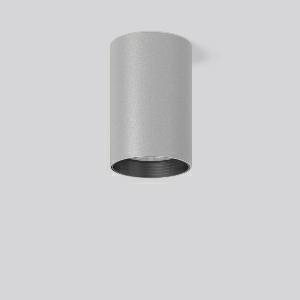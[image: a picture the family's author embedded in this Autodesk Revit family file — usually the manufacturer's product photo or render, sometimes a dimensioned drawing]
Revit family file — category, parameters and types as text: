
# Revit family: heledon_maxi_a_931243_004_76_f6dd
name_source: partatom
category: Lighting Fixtures
units: mm (PartAtom-declared; Revit-internal decimal feet)

## family parameters
Cut with Voids When Loaded = No
Host = Face
Light Source = No
Part Type = Normal
Room Calculation Point = No
Round Connector Dimension = Use Diameter
Shared = No

## types (1)
- HELEDON maxi A (1 x LED Modul 920 meat+, 1900 lm, 2000)
    Apparent Load = 33 VA
    Approval mark = CE
    CIE Flux Codes = 96 99 100 100 100
    Color Rendering = 90
    Color Temperature = 2000
    Default Elevation = 1800 mm
    Description = Series: HELEDON maxi
Cylindrical surface-mounted downlight. Housing: die-cast aluminium, powder-coated. Internal ceiling frame polycarbonate with bayonet mounting. Black plastic ring and recessed LED to prevent glare from the side. Optical assembly with lens made of plastic (polycarbonate) for the best homogeneous light distribution - can be changed without tools. Special LED for illumination of meat included. Suitable for Ceiling mounting. Easy installation with a separate ceiling frame with bayonet mounting and plug connection. Driver integrated. Connected via plug-in connector. High quality converter without flickering and stroboscopic effect. The following accessories can be mounted without use of tools: interchangeable lenses, decorative glasses, honeycomb louvre, clear and frosted diffusers, white interchangeable plastic ring. 
Colour: silver
Diameter: 123 mm
Height: 183 mm
Lamp: LED
Socket: without socket
Colour temperature: meat +
System power: 33 W
Rated luminous flux: 1900 lm
Luminous efficiency: 58 lm/W
Control gear: Converter, dimmable, DALI
Protection class: I
Type of protection: IP 20
    Height = 183 mm
    Lamp = 1 x LED Modul 920 meat+
    Lamp Light Flux = 1900 lm
    Lamp count = 1
    Length = 123 mm
    Lifetime = 50000 h
    Luminous efficacy = 58 lm/W
    Manufacturer = RZB
    ModVariant = No
    Model = 931243.004.76
    Mounting Place = Ceiling
    Mounting Type = Surface mounted
    Number of Poles = 1
    OnlyDefault = Yes
    Power Factor = 1
    Product Name = HELEDON maxi A
    Product group = Surface mounted downlights
    ProductGroupID = 302
    Protection Class = Protection class I
    Protection Degree = IP 20
    RLX_Detail_Level = 1
    RLX_Emergency_Light_Flux = 0 lm
    RLX_Emergency_Type = 0
    RLX_Emergency_Type_DB = No
    RlxData = <blob elided: 98293 chars, md5=9cc3c94e>
    Socket = socket
    Standby Power = 0 W
    System Light Flux = 1900 lm
    System Power = 33 W
    Type Comments = Product without accessories
    Type Image = 931193.004.jpg
    URL = http://relux.com
    VarID = ---
    Voltage = 230 V
    Voltage Range = 220-240 V
    Weight = 0.00 kg
    Width = 0 mm  [stored 0 ft]

note: [stored X ft] marks values corroborated as IEEE doubles in the binary element streams (Revit-internal decimal feet)

## geometry (parser evidence)
native form markers: Blend x4, Sweep x10
no freeform markers — native parametric forms only
